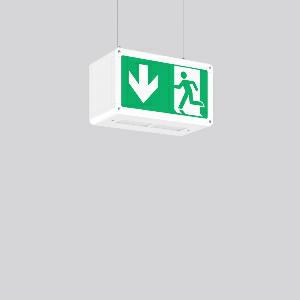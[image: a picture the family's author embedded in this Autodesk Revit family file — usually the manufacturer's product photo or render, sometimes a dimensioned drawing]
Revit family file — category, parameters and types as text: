
# Revit family: rechteck_seilpendel_671343_002_04_8a8e
name_source: partatom
category: Lighting Fixtures
units: mm (PartAtom-declared; Revit-internal decimal feet)

## family parameters
Cut with Voids When Loaded = No
Host = Face
Light Source = No
Part Type = Normal
Room Calculation Point = No
Round Connector Dimension = Use Diameter
Shared = No

## types (1)
- RECHTECK seilpendel
    Apparent Load = 0 VA
    Default Elevation = 1800 mm
    Description = Series: RECHTECK
Rectangular pendant luminaire in classic design. For escape route identification. Housing: aluminium, with plastic corner connectors. Display panels: plastic, opal, with motifs on one side/on both sides. Pendant luminaires (suspension provided on site) ready for connection to two suspension cables or chains. Driver integrated. Self-contained system with automatic self-test and feedback to the RZB monitoring system MULTIDIGIT. Please indicate legend number when placing your order! 
Colour: white
Length: 250 mm
Width: 125 mm
Height: 140 mm
Weight: 1.62 kg
Operating mode: maintained power mode
Viewing Distance: 21 m
Duration time: 3 h
Lamp: LED
Socket: without socket
Colour temperature: 6500K
Colour rendering index (CRI): 70
System power: 6.9 W
Control gear: Regulated power supply
Protection class: I
Type of protection: IP 44
    Height = 140 mm  [stored 0.459318 ft]
    Lamp = 0 x
    Length = 250 mm
    Luminous efficacy = 0 lm/W
    Manufacturer = RZB
    ModVariant = No
    Model = 671343.002.04
    Mounting Place = Ceiling
    Mounting Type = Pendant
    Number of Poles = 1
    OnlyDefault = Yes
    Power Factor = 1
    Product Name = RECHTECK seilpendel
    Product group = Pendant luminaires
    ProductGroupID = 902
    Protection Class = Protection class I
    Protection Degree = IP 44
    RLX_Detail_Level = 1
    RLX_Emergency_Light_Flux = 0 lm
    RLX_Emergency_Type = 0
    RLX_Emergency_Type_DB = No
    RlxData = <blob elided: 53977 chars, md5=50682cae>
    Standby Power = 0 W
    System Light Flux = 0 lm
    System Power = 0 W
    Type Comments = Product without accessories
    Type Image = 671359.002.jpg
    URL = http://relux.com
    VarID = ---
    Voltage = 230 V
    Voltage Range = 220-240 V
    Weight = 0.00 kg
    Width = 125 mm

note: [stored X ft] marks values corroborated as IEEE doubles in the binary element streams (Revit-internal decimal feet)

## geometry (parser evidence)
native form markers: Blend x4, Sweep x11
no freeform markers — native parametric forms only
